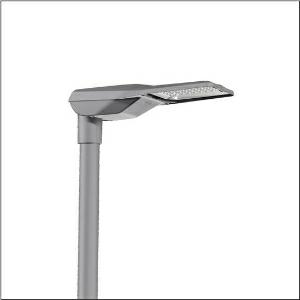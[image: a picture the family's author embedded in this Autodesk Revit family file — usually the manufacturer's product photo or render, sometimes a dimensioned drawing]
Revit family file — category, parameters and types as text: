
# Revit family: streetlight_sl_21_iq_mini___stw1_0a_5xe2e21d08hb_2a42
name_source: partatom
category: Lighting Fixtures
units: mm (PartAtom-declared; Revit-internal decimal feet)

## family parameters
Cut with Voids When Loaded = No
Host = Face
Light Source = No
Part Type = Normal
Room Calculation Point = No
Round Connector Dimension = Use Diameter
Shared = No

## types (1)
- --- (1 x LED, 7830 lm, 70.9 W, 2200K)
    Apparent Load = 71 VA
    CIE Flux Codes = 38 75 98 100 100
    Color Rendering = 70
    Color Temperature = 2200K
    Default Elevation = 1800 mm
    Description = Streetlight SL 21 iQ mini, mast luminaire, primary light control with lens, of PMMA, primary optical cover: cover, of toughened safety glass, transparent, light distribution: STW1.0a, light emission: direct distribution, primary light characteristic: asymmetric, installation type: post-top, side-entry, LED, High Power LED, rated luminous flux: 7.830lm, luminous efficacy: 110lm/W, light colour: 722, colour temperature: 2200K, control gear: iQ-Comfort, control: Auto-Match, Temp-Guard, Lumen-Switch, Night-Set, Smart-Wire, Light-Fading, Desk-Remote (wireless, voltage-free reading and setting of iQ features in the workshop via application-optimized NFC function/RFID function), optimised constant luminous flux control (CLO 2.0), pre-setting: linear dimming characteristic, mains connection: 220..240V, AC, 50/60Hz, start of lifetime: 71W, end of service life: 75W, reduction: 31W, luminaire housing, of diecast aluminium, powder-coated, Siteco® metallic grey (DB 702S), corrosivity category C5 mid according to DIN EN ISO 12944, please order mast flange separately, inclination adjustable: 0°, 5°, 10°, 15°, sealing non-destructively replaceable, multi-level sealing system, length: 628mm, width: 235mm, height: 110mm, mast flange for spigot size: 42mm (side-entry): 5XC10008XM4, 60/48mm (side-entry/post-top): 5XC10108XM2, 76/60mm (side-entry/post-top): 5XC10108XM1, mounting height: 4..8m, protection rating (complete): IP66, insulation class (complete): insulation class II (safety insulation), certification: CE, ENEC, ENEC+, VDE, impact resistance: IK10, permissible operating ambient temperature for outdoor applications: -40..+50°C, standard-compliant lighting for roads and squares, packaging unit: 1 piece

Light Distribution: STW1.0a
    Height = 110 mm
    Lamp = 1 x LED
    Lamp Light Flux = 7830 lm
    Lamp Power = 70.9 W
    Lamp count = 1
    Length = 625 mm
    Luminous efficacy = 110 lm/W
    Manufacturer = Siteco
    ModVariant = No
    Model = 5XE2E21D08HB
    Number of Poles = 1
    OnlyDefault = Yes
    Power Factor = 1
    Product Name = Streetlight SL 21 iQ mini | STW1.0a
    Product group = mast luminaire | pylon top
    ProductGroupID = 6100
    Protection Class = Protection class II
    Protection Degree = IP 66
    RLX_Detail_Level = 1
    RLX_Emergency_Light_Flux = 0 lm
    RLX_Emergency_Type = 0
    RLX_Emergency_Type_DB = No
    RlxData = <blob elided: 26285 chars, md5=4f63b1c5>
    Socket = socket
    Standby Power = 0 W
    System Light Flux = 7830 lm
    System Power = 71 W
    Type Comments = factory setting: luminous flux: 100 % | dim-lin: 254 | 711 mA
    Type Image = l_1003519.jpg
    URL = http://relux.com
    VarID = @adj_179477
    Voltage = 0 V
    Weight = 0.00 kg
    Width = 234 mm

## geometry (parser evidence)
native form markers: Blend x4, Sweep x12
no freeform markers — native parametric forms only
